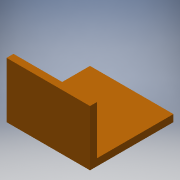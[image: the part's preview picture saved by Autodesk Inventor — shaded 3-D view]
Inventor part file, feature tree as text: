
AUTODESK INVENTOR PART (.ipt)
format: ipt  version: 2017 SP1 (Build 210196100, 196)  size: 103,424 bytes
history: native  units: in
note: dims shown in document units (in); Inventor stores cm internally (conversion verified against a paired STEP export)
features: extrude x2, sketch x2
ambient origin geometry x8: Origin, YZ Plane, XZ Plane, XY Plane, X Axis, Y Axis, Z Axis, Center Point
bodies: Solid1 (feature_tree)
feature tree (4):
  extrude  "Extrusion1"  Depth=0.125in
  extrude  "Extrusion2"  Depth=1.5in
  sketch  "Sketch1"  dims[d0=1.0in d1=0.125in]
  sketch  "Sketch2"  dims[d2=1.5in d3=0.0in d4=1.5in d5=0.375in d6=0.875in d7=0.75in d8=1.5in d9=0.0in]
